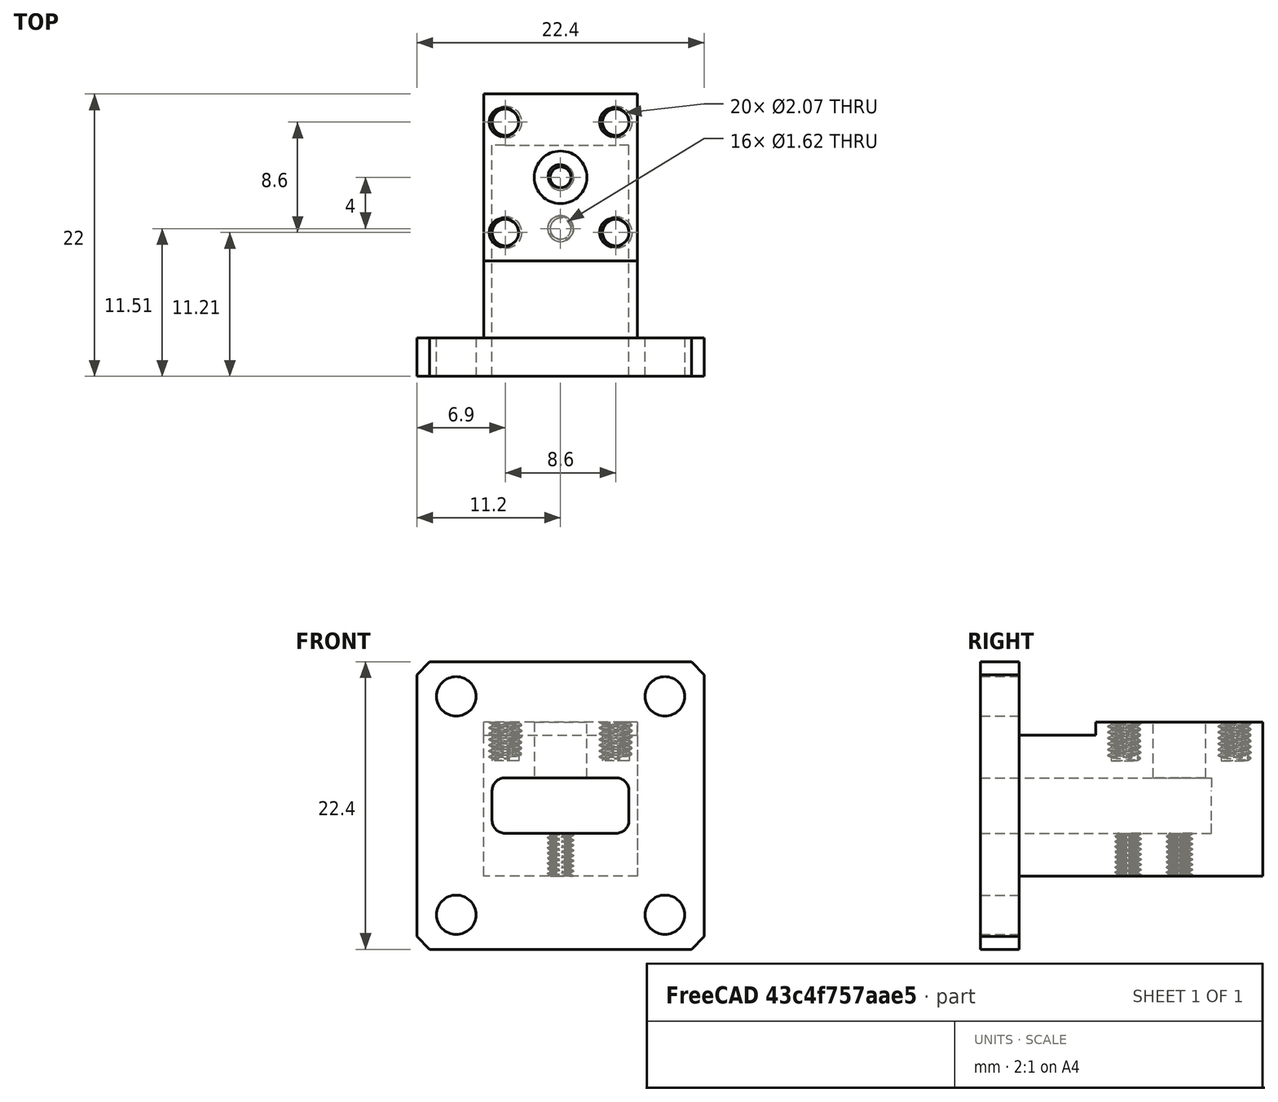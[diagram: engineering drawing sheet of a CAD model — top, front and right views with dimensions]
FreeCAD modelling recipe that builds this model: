
FCSTD DOCUMENT  (FreeCAD 1.0R38641 +468 (Git))
Label: WR42-SMA-narrow
License: All rights reserved
LicenseURL: https://en.wikipedia.org/wiki/All_rights_reserved
objects: Sketcher::SketchObject×7, PartDesign::Chamfer×4, PartDesign::Pad×3, TechDraw::DrawViewPart×3, TechDraw::DrawViewBalloon×3, PartDesign::Pocket×2, PartDesign::Hole×2, TechDraw::DrawSVGTemplate×1, PartDesign::Body×1, TechDraw::DrawPage×1
note: 48 computed .brp shape members not serialized (recipe doc carries the construction recipe); baked Part::Feature solids carry a one-line shape summary decoded from their .brp

FEATURE [Sketcher::SketchObject] Sketch
  ArcFitTolerance = 0
  AttachmentSupport = -> [XZ_Plane]
  FullyConstrained = true
  MakeInternals = false
  MapMode = 5
  Placement = pos=(0,0,0) rot=(1,0,0;1.5708rad)
  sketch-geometry (9):
    g0: LineSegment StartX=-11.2 StartY=11.2 StartZ=0 EndX=-11.2 EndY=-11.2 EndZ=0
    g1: LineSegment StartX=-11.2 StartY=-11.2 StartZ=0 EndX=11.2 EndY=-11.2 EndZ=0
    g2: LineSegment StartX=11.2 StartY=-11.2 StartZ=0 EndX=11.2 EndY=11.2 EndZ=0
    g3: LineSegment StartX=11.2 StartY=11.2 StartZ=0 EndX=-11.2 EndY=11.2 EndZ=0
    g4: GeomPoint [constr] X=0 Y=0 Z=0
    g5: Circle CenterX=-8.13 CenterY=8.51 CenterZ=0 NormalX=0 NormalY=0 NormalZ=1 AngleXU=0 Radius=1.535
    g6: Circle CenterX=8.13 CenterY=8.51 CenterZ=0 NormalX=0 NormalY=0 NormalZ=1 AngleXU=0 Radius=1.535
    g7: Circle CenterX=8.13 CenterY=-8.51 CenterZ=0 NormalX=0 NormalY=0 NormalZ=1 AngleXU=0 Radius=1.535
    g8: Circle CenterX=-8.13 CenterY=-8.51 CenterZ=0 NormalX=0 NormalY=0 NormalZ=1 AngleXU=0 Radius=1.535
  constraints (24):
    c: Coincident(g0,g1)
    c: Coincident(g1,g2)
    c: Coincident(g2,g3)
    c: Coincident(g3,g0)
    c: Horizontal(g1)
    c: Horizontal(g3)
    c: Vertical(g0)
    c: Vertical(g2)
    c: Symmetric(g1,g0,g4)
    c: Coincident(g4,g-1)
    c: DistanceY(g2,g2) = 22.4
    c: DistanceX(g3,g3) = 22.4
    c: Diameter(g5) = 3.07
    c: Equal(g5,g6)
    c: Equal(g5,g8)
    c: Equal(g5,g7)
    c: DistanceX(g4,g6) = 8.13
    c: DistanceX(g5,g4) = 8.13
    c: DistanceX(g8,g4) = 8.13
    c: DistanceX(g4,g7) = 8.13
    c: DistanceY(g4,g5) = 8.51
    c: DistanceY(g4,g6) = 8.51
    c: DistanceY(g7,g4) = 8.51
    c: DistanceY(g8,g4) = 8.51
FEATURE [PartDesign::Pad] Pad
  Direction = (0,-1,2e-16)
  Length = 3
  Length2 = 10
  Placement = pos=(0,0,0) rot=(1,0,0;1.5708rad)
  Profile = -> Sketch
  ReferenceAxis = -> Sketch [N_Axis]
  Suppressed = false
  Type = 0
FEATURE [PartDesign::Chamfer] Chamfer
  Angle = 45
  Base = -> Pad [Edge8]
  BaseFeature = -> Pad
  ChamferType = 0
  FlipDirection = false
  Placement = pos=(0,0,0) rot=(1,0,0;1.5708rad)
  Size = 1
  Size2 = 1
  SupportTransform = false
  Suppressed = false
  UseAllEdges = false
FEATURE [PartDesign::Chamfer] Chamfer001
  Angle = 45
  Base = -> Chamfer [Edge23]
  BaseFeature = -> Chamfer
  ChamferType = 0
  FlipDirection = false
  Placement = pos=(0,0,0) rot=(1,0,0;1.5708rad)
  Size = 1
  Size2 = 1
  SupportTransform = false
  Suppressed = false
  UseAllEdges = false
FEATURE [PartDesign::Chamfer] Chamfer002
  Angle = 45
  Base = -> Chamfer001 [Edge20]
  BaseFeature = -> Chamfer001
  ChamferType = 0
  FlipDirection = false
  Placement = pos=(0,0,0) rot=(1,0,0;1.5708rad)
  Size = 1
  Size2 = 1
  SupportTransform = false
  Suppressed = false
  UseAllEdges = false
FEATURE [PartDesign::Chamfer] Chamfer003
  Angle = 45
  Base = -> Chamfer002 [Edge19]
  BaseFeature = -> Chamfer002
  ChamferType = 0
  FlipDirection = false
  Placement = pos=(0,0,0) rot=(1,0,0;1.5708rad)
  Size = 1
  Size2 = 1
  SupportTransform = false
  Suppressed = false
  UseAllEdges = false
FEATURE [Sketcher::SketchObject] Sketch001
  ArcFitTolerance = 0
  AttachmentSupport = -> [Chamfer003]
  ExternalGeometry = -> [Chamfer003]
  FullyConstrained = true
  MakeInternals = false
  MapMode = 5
  Placement = pos=(0,0,0) rot=(-1,0,0;1.5708rad)
  sketch-geometry (5):
    g0: LineSegment StartX=-6 StartY=5.5 StartZ=0 EndX=-6 EndY=-5.5 EndZ=0
    g1: LineSegment StartX=-6 StartY=-5.5 StartZ=0 EndX=6 EndY=-5.5 EndZ=0
    g2: LineSegment StartX=6 StartY=-5.5 StartZ=0 EndX=6 EndY=5.5 EndZ=0
    g3: LineSegment StartX=6 StartY=5.5 StartZ=0 EndX=-6 EndY=5.5 EndZ=0
    g4: GeomPoint [constr] X=0 Y=0 Z=0
  constraints (12):
    c: Coincident(g0,g1)
    c: Coincident(g1,g2)
    c: Coincident(g2,g3)
    c: Coincident(g3,g0)
    c: Horizontal(g1)
    c: Horizontal(g3)
    c: Vertical(g0)
    c: Vertical(g2)
    c: Symmetric(g1,g0,g4)
    c: Coincident(g4,g-1)
    c: DistanceY(g2,g2) = 11
    c: DistanceX(g3,g3) = 12
FEATURE [PartDesign::Pad] Pad001
  BaseFeature = -> Chamfer003
  Direction = (0,1,2e-16)
  Length = 19
  Length2 = 10
  Placement = pos=(0,0,0) rot=(1,0,0;1.5708rad)
  Profile = -> Sketch001
  ReferenceAxis = -> Sketch001 [N_Axis]
  Suppressed = false
  Type = 0
FEATURE [Sketcher::SketchObject] Sketch002
  ArcFitTolerance = 0
  AttachmentSupport = -> [Pad001]
  FullyConstrained = true
  MakeInternals = false
  MapMode = 5
  Placement = pos=(0,-3,0) rot=(1,0,0;1.5708rad)
  sketch-geometry (13):
    g0: LineSegment StartX=-5.334 StartY=-1.159 StartZ=0 EndX=-5.334 EndY=1.159 EndZ=0
    g1: LineSegment StartX=-4.334 StartY=2.159 StartZ=0 EndX=4.334 EndY=2.159 EndZ=0
    g2: LineSegment StartX=5.334 StartY=1.159 StartZ=0 EndX=5.334 EndY=-1.159 EndZ=0
    g3: LineSegment StartX=4.334 StartY=-2.159 StartZ=0 EndX=-4.334 EndY=-2.159 EndZ=0
    g4: GeomPoint [constr] X=0 Y=0 Z=0
    g5: ArcOfCircle CenterX=-4.334 CenterY=1.159 CenterZ=0 NormalX=0 NormalY=0 NormalZ=1 AngleXU=0 Radius=1 StartAngle=1.5708 EndAngle=3.14159
    g6: GeomPoint [constr] X=-5.334 Y=2.159 Z=0
    g7: ArcOfCircle CenterX=4.334 CenterY=1.159 CenterZ=0 NormalX=0 NormalY=0 NormalZ=1 AngleXU=0 Radius=1 StartAngle=0 EndAngle=1.5708
    g8: GeomPoint [constr] X=5.334 Y=2.159 Z=0
    g9: ArcOfCircle CenterX=4.334 CenterY=-1.159 CenterZ=0 NormalX=0 NormalY=0 NormalZ=1 AngleXU=0 Radius=1 StartAngle=4.71239 EndAngle=6.28319
    g10: GeomPoint [constr] X=5.334 Y=-2.159 Z=0
    g11: ArcOfCircle CenterX=-4.334 CenterY=-1.159 CenterZ=0 NormalX=0 NormalY=0 NormalZ=1 AngleXU=0 Radius=1 StartAngle=3.14159 EndAngle=4.71239
    g12: GeomPoint [constr] X=-5.334 Y=-2.159 Z=0
  constraints (28):
    c: Horizontal(g1)
    c: Horizontal(g3)
    c: Vertical(g0)
    c: Vertical(g2)
    c: Symmetric(g8,g12,g4)
    c: Coincident(g4,g-1)
    c: PointOnObject(g6,g1)
    c: PointOnObject(g6,g0)
    c: Tangent(g1,g5) = 1.5708
    c: Tangent(g0,g5) = 1.5708
    c: PointOnObject(g8,g1)
    c: PointOnObject(g8,g2)
    c: Tangent(g1,g7) = 1.5708
    c: Tangent(g2,g7) = 1.5708
    c: PointOnObject(g10,g2)
    c: PointOnObject(g10,g3)
    c: Tangent(g2,g9) = 1.5708
    c: Tangent(g3,g9) = 1.5708
    c: PointOnObject(g12,g3)
    c: PointOnObject(g12,g0)
    c: Tangent(g3,g11) = 1.5708
    c: Tangent(g0,g11) = 1.5708
    c: Radius(g5) = 1
    c: Radius(g7) = 1
    c: Radius(g9) = 1
    c: Radius(g11) = 1
    c: DistanceX(g0,g2) = 10.668
    c: DistanceY(g3,g1) = 4.318
FEATURE [PartDesign::Pocket] Pocket
  BaseFeature = -> Pad001
  Direction = (0,1,-2e-16)
  Length = 18
  Length2 = 5
  Placement = pos=(0,0,0) rot=(1,0,0;1.5708rad)
  Profile = -> Sketch002
  ReferenceAxis = -> Sketch002 [N_Axis]
  Suppressed = false
  Type = 0
FEATURE [Sketcher::SketchObject] Sketch005
  ArcFitTolerance = 0
  AttachmentSupport = -> [Pocket]
  ExternalGeometry = -> [Pocket]
  FullyConstrained = true
  MakeInternals = false
  MapMode = 45
  Placement = pos=(2e-16,9.5,5.5) rot=(0,0,1;0rad)
  sketch-geometry (4):
    g0: LineSegment StartX=6 StartY=-3.5 StartZ=0 EndX=-6 EndY=-3.5 EndZ=0
    g1: LineSegment StartX=-6 StartY=-3.5 StartZ=0 EndX=-6 EndY=9.5 EndZ=0
    g2: LineSegment StartX=-6 StartY=9.5 StartZ=0 EndX=6 EndY=9.5 EndZ=0
    g3: LineSegment StartX=6 StartY=9.5 StartZ=0 EndX=6 EndY=-3.5 EndZ=0
  constraints (12):
    c: Coincident(g0,g1)
    c: Coincident(g1,g2)
    c: Coincident(g2,g3)
    c: Coincident(g3,g0)
    c: Horizontal(g0)
    c: Horizontal(g2)
    c: Vertical(g1)
    c: Vertical(g3)
    c: DistanceX(g2,g2) = 12
    c: DistanceX(g1,g-1) = 6
    c: DistanceY(g1,g-3) = 0
    c: DistanceY(g3,g3) = 13
FEATURE [PartDesign::Pad] Pad002
  BaseFeature = -> Pocket
  Direction = (0,0,1)
  Length = 1
  Length2 = 10
  Placement = pos=(0,0,0) rot=(1,0,0;1.5708rad)
  Profile = -> Sketch005
  ReferenceAxis = -> Sketch005 [N_Axis]
  Refine = true
  Suppressed = false
  Type = 0
FEATURE [Sketcher::SketchObject] Sketch006
  ArcFitTolerance = 0
  AttachmentSupport = -> [Pad002]
  ExternalGeometry = -> [Pad002]
  FullyConstrained = true
  MakeInternals = false
  MapMode = 5
  Placement = pos=(0,0,6.5) rot=(0,0,1;3.14159rad)
  sketch-geometry (1):
    g0: Circle CenterX=0 CenterY=-12.51 CenterZ=0 NormalX=0 NormalY=0 NormalZ=1 AngleXU=0 Radius=2.05
  constraints (3):
    c: PointOnObject(g0,g-2)
    c: Diameter(g0) = 4.1
    c: DistanceY(g-3,g0) = 2.49
FEATURE [PartDesign::Pocket] Pocket001
  BaseFeature = -> Pad002
  Direction = (0,0,-1)
  Length = 5
  Length2 = 5
  Placement = pos=(0,0,0) rot=(1,0,0;1.5708rad)
  Profile = -> Sketch006
  ReferenceAxis = -> Sketch006 [N_Axis]
  Suppressed = false
  Type = 2
FEATURE [Sketcher::SketchObject] Sketch007
  ArcFitTolerance = 0
  AttachmentSupport = -> [Pocket001]
  ExternalGeometry = -> [Pocket001]
  FullyConstrained = true
  MakeInternals = false
  MapMode = 5
  Placement = pos=(0,0,6.5) rot=(0,0,1;3.14159rad)
  sketch-geometry (4):
    g0: Circle CenterX=-4.3 CenterY=-8.21 CenterZ=0 NormalX=0 NormalY=0 NormalZ=1 AngleXU=0 Radius=1.025
    g1: Circle CenterX=4.3 CenterY=-8.21 CenterZ=0 NormalX=0 NormalY=0 NormalZ=1 AngleXU=0 Radius=1.025
    g2: Circle CenterX=4.3 CenterY=-16.81 CenterZ=0 NormalX=0 NormalY=0 NormalZ=1 AngleXU=0 Radius=1.025
    g3: Circle CenterX=-4.3 CenterY=-16.81 CenterZ=0 NormalX=0 NormalY=0 NormalZ=1 AngleXU=0 Radius=1.025
  constraints (12):
    c: Diameter(g0) = 2.05
    c: Equal(g1,g0)
    c: Equal(g0,g2)
    c: Equal(g0,g3)
    c: DistanceX(g0,g-3) = 4.3
    c: DistanceY(g-3,g0) = 4.3
    c: DistanceX(g-3,g1) = 4.3
    c: DistanceX(g-3,g2) = 4.3
    c: DistanceX(g3,g-3) = 4.3
    c: DistanceY(g-3,g1) = 4.3
    c: DistanceY(g2,g-3) = 4.3
    c: DistanceY(g3,g-3) = 4.3
FEATURE [PartDesign::Hole] Hole
  BaseFeature = -> Pocket001
  CustomThreadClearance = 0
  Depth = 3
  DepthType = 0
  Diameter = 2.07
  DrillForDepth = false
  DrillPoint = 0
  DrillPointAngle = 118
  HoleCutCountersinkAngle = 90
  HoleCutCustomValues = false
  HoleCutDepth = 0
  HoleCutDiameter = 6.1
  HoleCutType = 0
  ModelThread = true
  Placement = pos=(0,0,0) rot=(1,0,0;1.5708rad)
  Profile = -> Sketch007
  Suppressed = false
  Tapered = false
  TaperedAngle = 90
  ThreadClass = 0
  ThreadDepth = 3
  ThreadDepthType = 0
  ThreadDirection = 0
  ThreadFit = 0
  ThreadSize = 8
  ThreadType = 1
  Threaded = true
  UseCustomThreadClearance = false
FEATURE [TechDraw::DrawSVGTemplate] Template
  EditableTexts = Drawing_number=01; FC-Date=31/3/2025; FC-SC=2 : 1; FC-SH=01; FC-Title=WR42-SMA-narrow; Subtitle=Threads and precision perspective; Weight=n/a
  Height = 210
  Orientation = 1
  Template = <path>
  Width = 297
FEATURE [TechDraw::DrawViewPart] View  label="Front"
  CoarseView = false
  Direction = (0,-1,0)
  Focus = 100
  HardHidden = false
  IsoCount = 0
  IsoHidden = false
  IsoVisible = false
  LockPosition = false
  Perspective = false
  Rotation = 0
  Scale = 2
  ScaleType = 2
  ScrubCount = 0
  SeamHidden = false
  SeamVisible = false
  SmoothHidden = false
  SmoothVisible = true
  X = 73.0258
  XDirection = (1,0,0)
  Y = 63.0699
FEATURE [TechDraw::DrawViewBalloon] Balloon
  BubbleShape = 6
  EndType = 0
  EndTypeScale = 1
  KinkLength = 5
  LockPosition = false
  OriginX = 0.700083
  OriginY = 0.0873544
  Rotation = 0
  ScaleType = 0
  ShapeScale = 1
  SourceView = -> View
  Text = internal dimensions high precision
  TextWrapLen = -1
  X = 43.3706
  Y = 2.40017
FEATURE [Sketcher::SketchObject] Sketch008
  ArcFitTolerance = 1e-06
  FullyConstrained = true
  MakeInternals = false
  MapMode = 5
  Placement = pos=(0,0,-5.5) rot=(1,0,0;3.14159rad)
  sketch-geometry (2):
    g0: Circle CenterX=0 CenterY=-12.51 CenterZ=0 NormalX=0 NormalY=0 NormalZ=1 AngleXU=0 Radius=0.75
    g1: Circle CenterX=0 CenterY=-8.51 CenterZ=0 NormalX=0 NormalY=0 NormalZ=1 AngleXU=0 Radius=0.75
  constraints (5):
    c: Diameter(g0) = 1.5
    c: Coincident(g0,g-3)
    c: PointOnObject(g1,g-2)
    c: Equal(g0,g1)
    c: DistanceY(g0,g1) = 4
FEATURE [PartDesign::Hole] Hole001
  BaseFeature = -> Hole
  CustomThreadClearance = 0
  Depth = 4
  DepthType = 0
  Diameter = 1.619
  DrillForDepth = false
  DrillPoint = 1
  DrillPointAngle = 118
  HoleCutCountersinkAngle = 90
  HoleCutCustomValues = false
  HoleCutDepth = 0
  HoleCutDiameter = 6.1
  HoleCutType = 0
  ModelThread = true
  Placement = pos=(0,0,0) rot=(1,0,0;1.5708rad)
  Profile = -> Sketch008
  Refine = true
  Suppressed = false
  Tapered = false
  TaperedAngle = 90
  ThreadClass = 0
  ThreadDepth = 4
  ThreadDepthType = 0
  ThreadDirection = 0
  ThreadFit = 0
  ThreadSize = 6
  ThreadType = 1
  Threaded = true
  UseCustomThreadClearance = false
FEATURE [PartDesign::Body] Body
  AllowCompound = false
  Group = -> [Sketch,Pad,Chamfer,Chamfer001,Chamfer002,Chamfer003,Sketch001,Pad001,Sketch002,Pocket,Sketch005,Pad002,Sketch006,Pocket001,Sketch007,Hole,Sketch008,Hole001]
  Origin = -> Origin
  Tip = -> Hole001
FEATURE [TechDraw::DrawViewPart] View001  label="Top"
  CoarseView = false
  Direction = (0,0,1)
  Focus = 100
  HardHidden = false
  IsoCount = 0
  IsoHidden = false
  IsoVisible = false
  LockPosition = false
  Perspective = false
  Rotation = 0
  Scale = 2
  ScaleType = 2
  ScrubCount = 0
  SeamHidden = false
  SeamVisible = false
  SmoothHidden = false
  SmoothVisible = true
  Source = -> [Hole001]
  X = 74.4235
  XDirection = (1,0,0)
  Y = 144.484
FEATURE [TechDraw::DrawViewPart] View002  label="Bottom"
  CoarseView = false
  Direction = (0,0,-1)
  Focus = 100
  HardHidden = false
  IsoCount = 0
  IsoHidden = false
  IsoVisible = false
  LockPosition = false
  Perspective = false
  Rotation = 0
  Scale = 2
  ScaleType = 2
  ScrubCount = 0
  SeamHidden = false
  SeamVisible = false
  SmoothHidden = false
  SmoothVisible = true
  Source = -> [Hole001]
  X = 225.372
  XDirection = (1,0,0)
  Y = 152.521
FEATURE [TechDraw::DrawViewBalloon] Balloon001
  BubbleShape = 6
  EndType = 0
  EndTypeScale = 1
  KinkLength = 5
  LockPosition = false
  OriginX = 0.525374
  OriginY = -4.28037
  Rotation = 0
  ScaleType = 0
  ShapeScale = 1
  SourceView = -> View002
  Text = 2 x M2 0,4
  TextWrapLen = -1
  X = 15.9413
  Y = -25.3785
FEATURE [TechDraw::DrawViewBalloon] Balloon002
  BubbleShape = 6
  EndType = 0
  EndTypeScale = 1
  KinkLength = 5
  LockPosition = false
  OriginX = -4.01705
  OriginY = 9.34692
  Rotation = 0
  ScaleType = 0
  ShapeScale = 1
  SourceView = -> View001
  Text = 4 x M2.5 0,45
  TextWrapLen = -1
  X = 21.0079
  Y = 19.1722
FEATURE [TechDraw::DrawPage] Page  label="2D drawing"
  KeepUpdated = true
  NextBalloonIndex = 4
  ProjectionType = 0
  Template = -> Template
  Views = -> [View,View001,View002,Balloon,Balloon001,Balloon002]
note: 1 file-system path scrubbed to <path> (originals preserved in the JSON sidecar)
